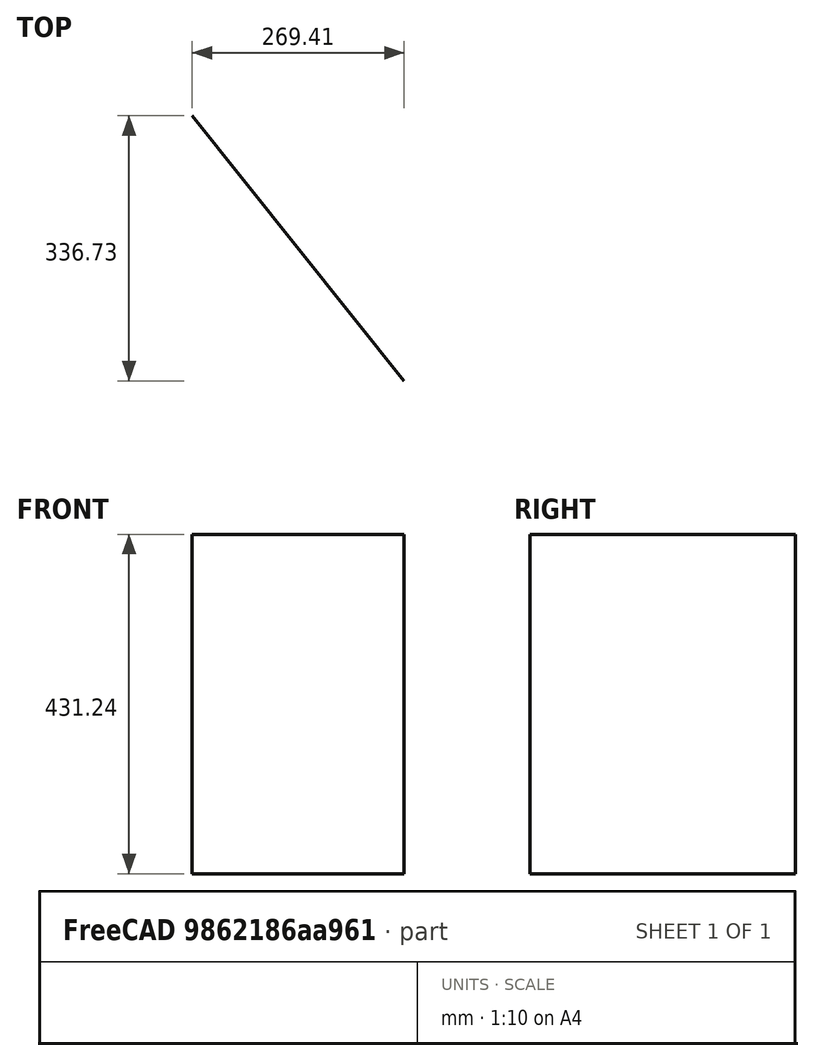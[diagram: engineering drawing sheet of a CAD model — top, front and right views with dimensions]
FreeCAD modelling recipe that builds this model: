
FCSTD DOCUMENT  (FreeCAD 0.16R4925 (Git))
Label: fahrrad
License: All rights reserved
LicenseURL: http://en.wikipedia.org/wiki/All_rights_reserved
objects: Sketcher::SketchObject×9, App::DocumentObjectGroup×2, Part::Feature×1
note: 10 computed .brp shape members not serialized (recipe doc carries the construction recipe); baked Part::Feature solids carry a one-line shape summary decoded from their .brp

FEATURE [Sketcher::SketchObject] Sketch
  sketch-geometry (5):
    g0: LineSegment StartX=0 StartY=0 StartZ=0 EndX=-409.104 EndY=435.926 EndZ=0
    g1: LineSegment StartX=-380.814 StartY=523.456 StartZ=0 EndX=-426.982 EndY=380.613 EndZ=0
    g2: LineSegment StartX=-394.525 StartY=481.032 StartZ=0 EndX=61.836 EndY=288.394 EndZ=0
    g3: LineSegment StartX=0 StartY=0 StartZ=0 EndX=77.9974 EndY=363.768 EndZ=0
    g4: GeomPoint [constr] X=-550 Y=0 Z=0
  constraints (9):
    c: Coincident(g3,g-1)
    c: PointOnObject(g2,g3)
    c: Coincident(g0,g-1)
    c: PointOnObject(g0,g1)
    c: PointOnObject(g2,g1)
    c: PointOnObject(g4,g-1)
    c: PointOnObject(g4,g1)
    c: DistanceX(g-1,g4) = -550
    c: Distance(g1,g4) = 400
FEATURE [Sketcher::SketchObject] Sketch001
  Placement = pos=(0,0,0) rot=(1,0,0;1.5708rad)
  sketch-geometry (1):
    g0: LineSegment StartX=0 StartY=40 StartZ=0 EndX=0 EndY=-40 EndZ=0
  constraints (4):
    c: PointOnObject(g0,g-2)
    c: Vertical(g0)
    c: DistanceY(g-1,g0) = -40
    c: DistanceY(g-1,g0) = 40
FEATURE [Sketcher::SketchObject] Sketch002
  sketch-geometry (3):
    g0: Circle CenterX=-506.1 CenterY=81.4881 CenterZ=0 NormalX=0 NormalY=0 NormalZ=1 Radius=20
    g1: Circle CenterX=-506.1 CenterY=81.4881 CenterZ=0 NormalX=0 NormalY=0 NormalZ=1 Radius=18
    g2: GeomPoint [constr] X=-506.1 Y=81.4881 Z=0
  constraints (4):
    c: Radius(g0) = 20
    c: Coincident(g1,g0)
    c: Radius(g1) = 18
    c: Coincident(g2,g0)
FEATURE [Sketcher::SketchObject] Sketch003
  Placement = pos=(0,0,0) rot=(1,0,0;1.5708rad)
  sketch-geometry (4):
    g0: LineSegment StartX=0 StartY=-15.8886 StartZ=0 EndX=45.0082 EndY=-34.5382 EndZ=0
    g1: LineSegment StartX=45.0082 StartY=-34.5382 StartZ=0 EndX=295.618 EndY=-55 EndZ=0
    g2: LineSegment StartX=0 StartY=15.8886 StartZ=0 EndX=45.0082 EndY=34.5382 EndZ=0
    g3: LineSegment StartX=45.0082 StartY=34.5382 StartZ=0 EndX=295.618 EndY=55 EndZ=0
  constraints (8):
    c: PointOnObject(g0,g-2)
    c: Coincident(g0,g1)
    c: DistanceY(g-1,g1) = -55
    c: PointOnObject(g2,g-2)
    c: Coincident(g2,g3)
    c: Symmetric(g2,g0,g-1)
    c: Symmetric(g1,g3,g-1)
    c: Symmetric(g2,g0,g-1)
FEATURE [Sketcher::SketchObject] Sketch004
  sketch-geometry (9):
    g0: LineSegment StartX=-436.641 StartY=129.083 StartZ=0 EndX=-424.641 EndY=129.083 EndZ=0
    g1: LineSegment StartX=-424.641 StartY=129.083 StartZ=0 EndX=-424.641 EndY=113.083 EndZ=0
    g2: LineSegment StartX=-424.641 StartY=113.083 StartZ=0 EndX=-436.641 EndY=113.083 EndZ=0
    g3: LineSegment StartX=-436.641 StartY=113.083 StartZ=0 EndX=-436.641 EndY=129.083 EndZ=0
    g4: LineSegment StartX=-435.641 StartY=128.083 StartZ=0 EndX=-425.641 EndY=128.083 EndZ=0
    g5: LineSegment StartX=-425.641 StartY=128.083 StartZ=0 EndX=-425.641 EndY=114.083 EndZ=0
    g6: LineSegment StartX=-425.641 StartY=114.083 StartZ=0 EndX=-435.641 EndY=114.083 EndZ=0
    g7: LineSegment StartX=-435.641 StartY=114.083 StartZ=0 EndX=-435.641 EndY=128.083 EndZ=0
    g8: GeomPoint [constr] X=-430.641 Y=121.083 Z=0
  constraints (24):
    c: Coincident(g0,g1)
    c: Coincident(g1,g2)
    c: Coincident(g2,g3)
    c: Coincident(g3,g0)
    c: Horizontal(g0)
    c: Horizontal(g2)
    c: Vertical(g1)
    c: Vertical(g3)
    c: Coincident(g4,g5)
    c: Coincident(g5,g6)
    c: Coincident(g6,g7)
    c: Coincident(g7,g4)
    c: Horizontal(g4)
    c: Horizontal(g6)
    c: Vertical(g5)
    c: Vertical(g7)
    c: DistanceX(g5,g1) = 1
    c: DistanceX(g2,g6) = 1
    c: DistanceY(g1,g5) = 1
    c: DistanceY(g4,g0) = 1
    c: DistanceX(g8,g4) = -5
    c: DistanceX(g8,g4) = 5
    c: DistanceY(g8,g5) = -7
    c: DistanceY(g8,g4) = 7
FEATURE [Part::Feature] WorkPlane
  Placement = pos=(134.705,-168.361,-215.618) rot=(0,0,1;0rad)
  shape: bbox 269.4 x 336.7 x 431.2 mm, 1 faces, 0 solids (baked)
FEATURE [Sketcher::SketchObject] Sketch005
  Placement = pos=(314.943,-24.1531,-215.618) rot=(0.321756,0.669505,0.669505;2.519rad)
  Support = -> WorkPlane [Face1]
  sketch-geometry (5):
    g0: LineSegment StartX=397.238 StartY=223.328 StartZ=0 EndX=343.225 EndY=256.898 EndZ=0
    g1: LineSegment StartX=343.225 StartY=256.898 StartZ=0 EndX=30.4736 EndY=270.517 EndZ=0
    g2: LineSegment StartX=397.238 StartY=207.839 StartZ=0 EndX=343.225 EndY=174.269 EndZ=0
    g3: LineSegment StartX=343.225 StartY=174.269 StartZ=0 EndX=30.4736 EndY=160.651 EndZ=0
    g4: LineSegment [constr] StartX=0 StartY=215.584 StartZ=0 EndX=487.153 EndY=215.584 EndZ=0
  constraints (7):
    c: Coincident(g0,g1)
    c: Coincident(g2,g3)
    c: PointOnObject(g4,g-2)
    c: Horizontal(g4)
    c: Symmetric(g2,g0,g4)
    c: Symmetric(g2,g0,g4)
    c: Symmetric(g3,g1,g4)
FEATURE [App::DocumentObjectGroup] WorkPlanes
  Group = -> [WorkPlane,Sketch005]
FEATURE [App::DocumentObjectGroup] WorkFeatures
  Group = -> [WorkPlanes]
FEATURE [Sketcher::SketchObject] Sketch006
  sketch-geometry (3):
    g0: Circle CenterX=-375.344 CenterY=78.1925 CenterZ=0 NormalX=0 NormalY=0 NormalZ=1 Radius=14
    g1: Circle CenterX=-375.344 CenterY=78.1925 CenterZ=0 NormalX=0 NormalY=0 NormalZ=1 Radius=13
    g2: GeomPoint [constr] X=-375.344 Y=78.1925 Z=0
  constraints (4):
    c: Coincident(g1,g0)
    c: Radius(g1) = 13
    c: Radius(g0) = 14
    c: Coincident(g2,g0)
FEATURE [Sketcher::SketchObject] Sketch007
  sketch-geometry (3):
    g0: Circle CenterX=-443.749 CenterY=84.0798 CenterZ=0 NormalX=0 NormalY=0 NormalZ=1 Radius=7
    g1: Circle CenterX=-443.749 CenterY=84.0798 CenterZ=0 NormalX=0 NormalY=0 NormalZ=1 Radius=6
    g2: GeomPoint [constr] X=-443.749 Y=84.0798 Z=0
  constraints (4):
    c: Coincident(g1,g0)
    c: Radius(g1) = 6
    c: Radius(g0) = 7
    c: Coincident(g2,g0)
FEATURE [Sketcher::SketchObject] Sketch008
  sketch-geometry (3):
    g0: Circle CenterX=-433.392 CenterY=9.79779 CenterZ=0 NormalX=0 NormalY=0 NormalZ=1 Radius=38
    g1: Circle CenterX=-433.392 CenterY=9.79779 CenterZ=0 NormalX=0 NormalY=0 NormalZ=1 Radius=40
    g2: GeomPoint [constr] X=-433.392 Y=9.79779 Z=0
  constraints (4):
    c: Coincident(g1,g0)
    c: Coincident(g2,g0)
    c: Radius(g1) = 40
    c: Radius(g0) = 38
